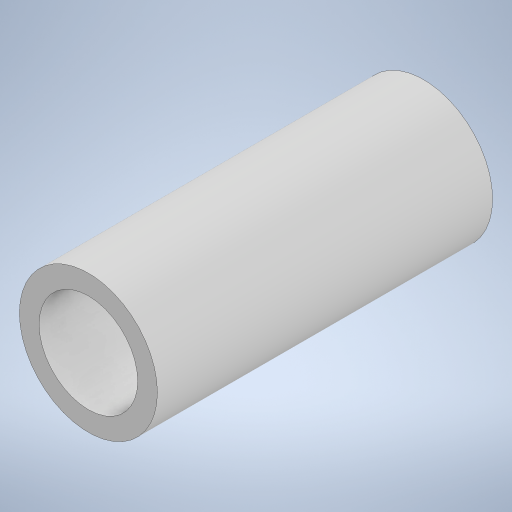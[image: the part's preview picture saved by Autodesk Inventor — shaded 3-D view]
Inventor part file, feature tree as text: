
AUTODESK INVENTOR PART (.ipt)
format: ipt  version: 2023.3 (Build 273359000, 359)  size: 208,896 bytes
history: native  units: in
note: dims shown in document units (in); Inventor stores cm internally (conversion verified against a paired STEP export)
features: extrude x1, sketch x1
ambient origin geometry x8: Origin, YZ Plane, XZ Plane, XY Plane, X Axis, Y Axis, Z Axis, Center Point
bodies: Solid1 (feature_tree)
feature tree (2):
  extrude  "Extrusion1"  Depth=0.6693in
  sketch  "Sketch1"  dims[d0=0.1969in d1=0.0394in d2=0.6693in d3=0.0in d4=0.5in d5=0.0344in d6=0.5in d7=0.0344in]
